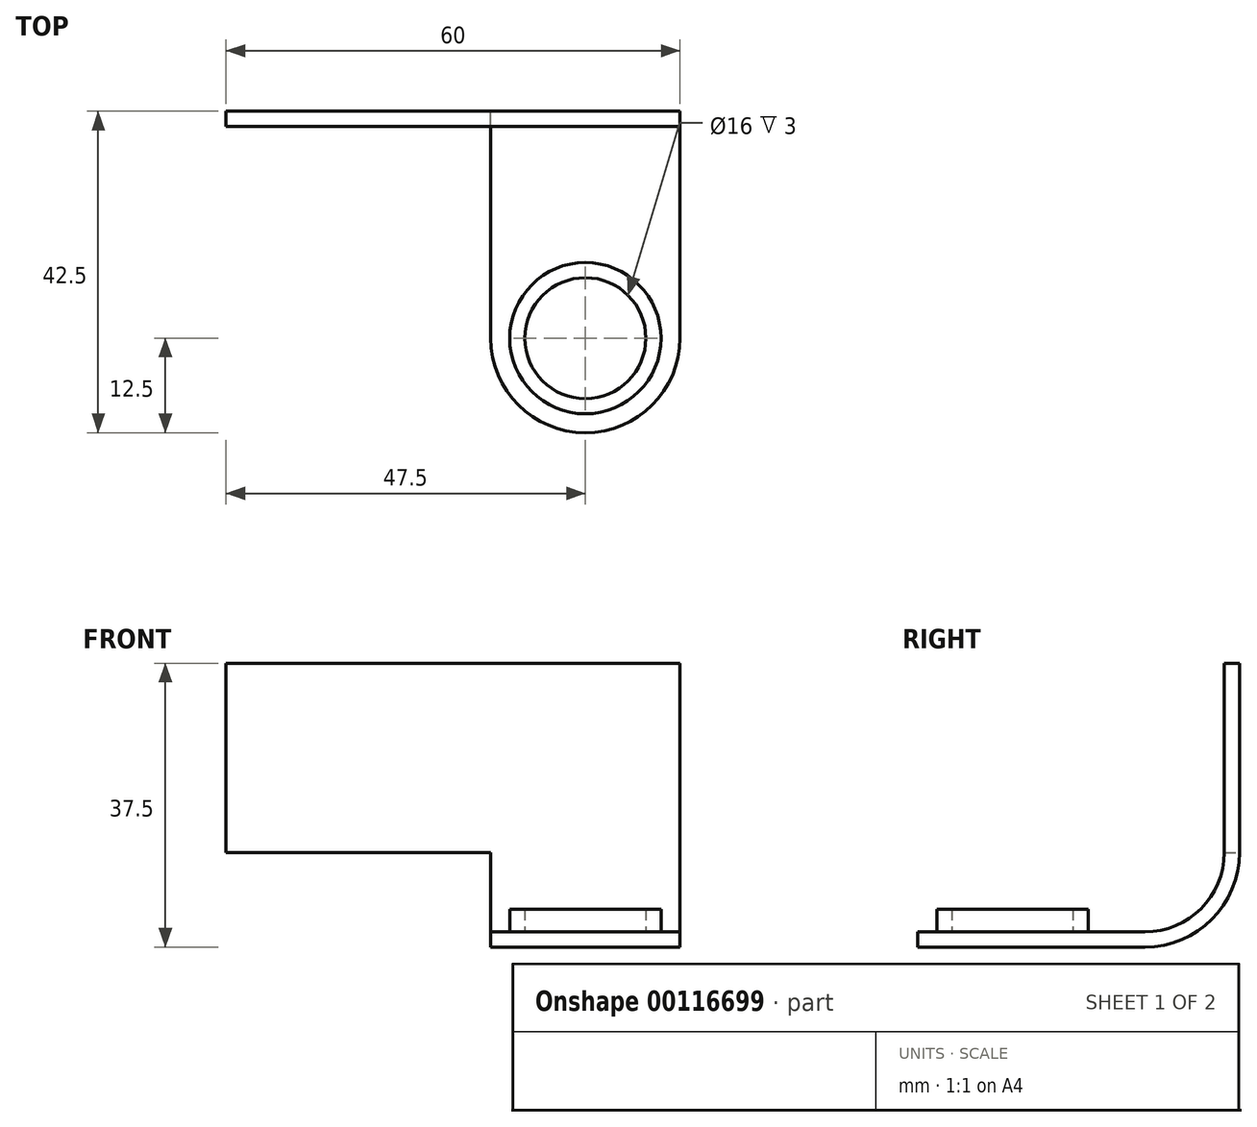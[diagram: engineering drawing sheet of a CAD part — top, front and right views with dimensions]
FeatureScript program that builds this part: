
annotation { "Feature Type Name" : "Feature", "Feature Type Description" : "" }
export const myFeature = defineFeature(function(context is Context, id is Id, definition is map)
    precondition{}
    {
        {
            var Q0;
            Q0=qCreatedBy(makeId("Front.planeOp"),FACE);
            var sketch = newSketch(context, id + "F0", { "sketchPlane" : qUnion([Q0])});
            skLineSegment(sketch, "E0.bottom", {"start": v(-47.5, 0) * mm, "end": v(12.5, 0) * mm});
            skLineSegment(sketch, "E0.top", {"start": v(-47.5, 25) * mm, "end": v(12.5, 25) * mm});
            skLineSegment(sketch, "E0.left", {"start": v(-47.5, 0) * mm, "end": v(-47.5, 25) * mm});
            skLineSegment(sketch, "E0.right", {"start": v(12.5, 0) * mm, "end": v(12.5, 25) * mm});
            skLineSegment(sketch, "E1", {"start": v(0, 0) * mm, "end": v(0, 38.04) * mm, "construction": true});
            skSolve(sketch);
        }
        {
            var Q0;
            Q0 = qSketchRegion(id + "F0", true);
            extrude(context, id + "F1", {"entities" : qUnion([Q0]), "depth" : 2 * mm});
        }
        {
            var Q0;
            Q0=qCreatedBy(makeId("Right.planeOp"),FACE);
            var sketch = newSketch(context, id + "F2", { "sketchPlane" : qUnion([Q0])});
            skArc(sketch, "E2", {"start": v(-12.5, -12.5) * mm, "mid": v(-3.66, -8.84) * mm, "end": v(0, 0) * mm});
            skLineSegment(sketch, "E3", {"start": v(-12.5, -12.5) * mm, "end": v(-42.5, -12.5) * mm});
            skArc(sketch, "E4.0", {"start": v(-12.5, -10.5) * mm, "mid": v(-5.08, -7.42) * mm, "end": v(-2, 0) * mm});
            skLineSegment(sketch, "E4.1", {"start": v(-12.5, -10.5) * mm, "end": v(-42.5, -10.5) * mm});
            skLineSegment(sketch, "E5", {"start": v(-2, 0) * mm, "end": v(0, 0) * mm});
            skLineSegment(sketch, "E6", {"start": v(-42.5, -12.5) * mm, "end": v(-42.5, -10.5) * mm});
            skSolve(sketch);
        }
        {
            var Q0;
            Q0 = qSketchRegion(id + "F2", true);
            extrude(context, id + "F3", {"entities" : qUnion([Q0]), "operationType" : NewBodyOperationType.ADD, "endBound" : BoundingType.SYMMETRIC, "depth" : 25 * mm});
        }
        {
            var Q0;
            Q0=makeQuery(id+"F3.opExtrude","CAP_EDGE",EDGE,{"disambiguationData":[OSD([sQuery(id+"F2.wireOp",EDGE,"E6")])],"isStart":true});
            var Q1;
            Q1=makeQuery(id+"F3.opExtrude","CAP_EDGE",EDGE,{"disambiguationData":[OSD([sQuery(id+"F2.wireOp",EDGE,"E6")])],"isStart":false});
            fillet(context, id + "F4", {"entities" : qUnion([Q0, Q1]), "radius" : 12.5 * mm, "tangentPropagation" : true, "allowEdgeOverflow" : false});
        }
        {
            var Q0;
            Q0=makeQuery(id+"F3.opExtrude","SWEPT_FACE",FACE,{"disambiguationData":[OSD([sQuery(id+"F2.wireOp",EDGE,"E4.1")])]});
            var sketch = newSketch(context, id + "F5", { "sketchPlane" : qUnion([Q0])});
            skCircle(sketch, "E7", {"center": v(0, -30) * mm, "radius": 8 * mm});
            skCircle(sketch, "E8.0", {"center": v(0, -30) * mm, "radius": 10 * mm});
            skSolve(sketch);
        }
        {
            var Q0;
            Q0 = qSketchRegion(id + "F5", true);
            extrude(context, id + "F6", {"entities" : qUnion([Q0]), "operationType" : NewBodyOperationType.ADD, "depth" : 3 * mm});
        }
    });
